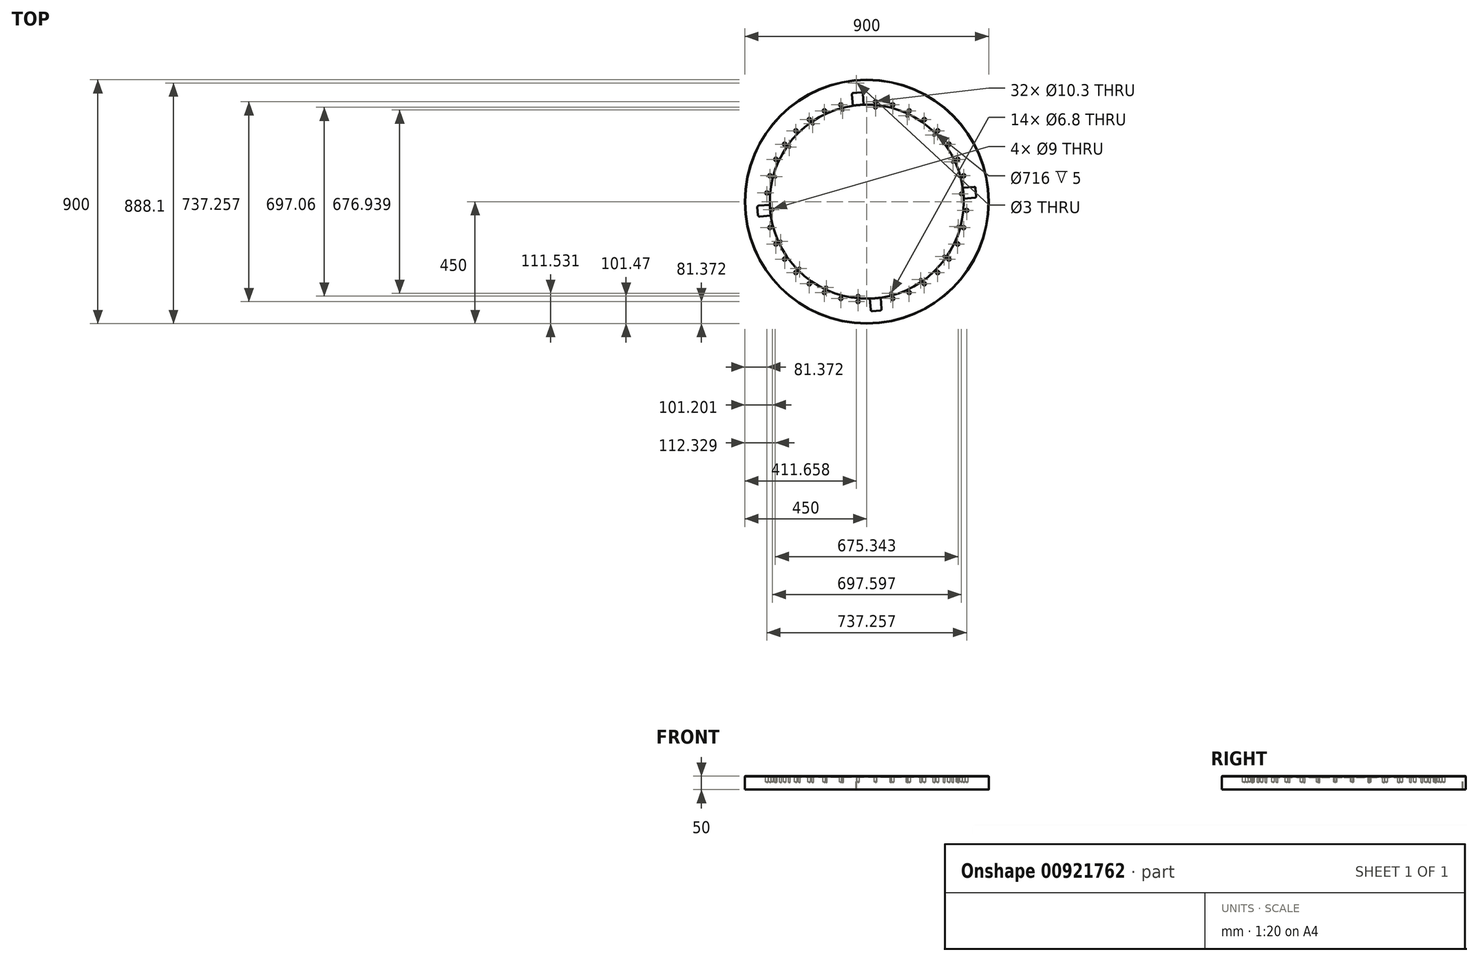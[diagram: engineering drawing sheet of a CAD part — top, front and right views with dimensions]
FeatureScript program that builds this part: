
annotation { "Feature Type Name" : "Feature", "Feature Type Description" : "" }
export const myFeature = defineFeature(function(context is Context, id is Id, definition is map)
    precondition{}
    {
        {
            var Q0;
            Q0=qCreatedBy(makeId("Front.planeOp"),FACE);
            var sketch = newSketch(context, id + "F0", { "sketchPlane" : qUnion([Q0])});
            skLineSegment(sketch, "E0", {"start": v(0, 121.97) * mm, "end": v(0, -124.32) * mm, "construction": true});
            skSolve(sketch);
        }
        {
            var Q0;
            Q0=qCreatedBy(makeId("Top.planeOp"),FACE);
            var sketch = newSketch(context, id + "F1", { "sketchPlane" : qUnion([Q0])});
            skLineSegment(sketch, "E1", {"start": v(-554.57, 0) * mm, "end": v(555.42, 0) * mm, "construction": true});
            skLineSegment(sketch, "E2", {"start": v(0, 588.1) * mm, "end": v(0, -621.05) * mm, "construction": true});
            skSolve(sketch);
        }
        {
            var Q0;
            Q0=qCreatedBy(makeId("Top.planeOp"),FACE);
            var sketch = newSketch(context, id + "F2", { "sketchPlane" : qUnion([Q0])});
            skCircle(sketch, "E3", {"center": v(0, 0) * mm, "radius": 450 * mm});
            skSolve(sketch);
        }
        {
            var Q0;
            Q0 = qSketchRegion(id + "F2", true);
            extrude(context, id + "F3", {"entities" : qUnion([Q0]), "oppositeDirection" : true, "depth" : 50 * mm, "offsetDistance" : 25 * mm});
        }
        {
            var Q0;
            Q0=makeQuery(id+"F3.opExtrude","CAP_FACE",FACE,{"disambiguationData":[OSD([sQuery(id+"F2.wireOp",EDGE,"E3")])],"isStart":true});
            var sketch = newSketch(context, id + "F4", { "sketchPlane" : qUnion([Q0])});
            skCircle(sketch, "E4", {"center": v(0, 0) * mm, "radius": 358 * mm});
            skSolve(sketch);
        }
        {
            var Q0;
            Q0 = qSketchRegion(id + "F4", true);
            extrude(context, id + "F5", {"entities" : qUnion([Q0]), "operationType" : NewBodyOperationType.REMOVE, "oppositeDirection" : true, "depth" : 5 * mm, "offsetDistance" : 25 * mm});
        }
        {
            var Q0;
            Q0=qCreatedBy(makeId("Top.planeOp"),FACE);
            var sketch = newSketch(context, id + "F6", { "sketchPlane" : qUnion([Q0])});
            skCircle(sketch, "E5", {"center": v(32.04, 348.53) * mm, "radius": 4.5 * mm});
            skPoint(sketch, "E6.center", {"position": v(0, 0) * mm});
            skCircle(sketch, "E7.1.0", {"center": v(-89.1, 338.47) * mm, "radius": 4.5 * mm});
            skCircle(sketch, "E7.2.0", {"center": v(-199.49, 287.58) * mm, "radius": 4.5 * mm});
            skCircle(sketch, "E7.3.0", {"center": v(-285.82, 202.01) * mm, "radius": 4.5 * mm});
            skCircle(sketch, "E7.4.0", {"center": v(-337.67, 92.07) * mm, "radius": 4.5 * mm});
            skCircle(sketch, "E7.5.0", {"center": v(-348.8, -28.97) * mm, "radius": 4.5 * mm});
            skCircle(sketch, "E7.6.0", {"center": v(-317.86, -146.52) * mm, "radius": 4.5 * mm});
            skCircle(sketch, "E7.7.0", {"center": v(-248.57, -246.4) * mm, "radius": 4.5 * mm});
            skCircle(sketch, "E7.8.0", {"center": v(-149.31, -316.55) * mm, "radius": 4.5 * mm});
            skCircle(sketch, "E7.9.0", {"center": v(-32.04, -348.53) * mm, "radius": 4.5 * mm});
            skCircle(sketch, "E7.10.0", {"center": v(89.1, -338.47) * mm, "radius": 4.5 * mm});
            skCircle(sketch, "E7.11.0", {"center": v(199.49, -287.58) * mm, "radius": 4.5 * mm});
            skCircle(sketch, "E7.12.0", {"center": v(285.82, -202.01) * mm, "radius": 4.5 * mm});
            skCircle(sketch, "E7.13.0", {"center": v(337.67, -92.07) * mm, "radius": 4.5 * mm});
            skCircle(sketch, "E7.14.0", {"center": v(348.8, 28.97) * mm, "radius": 4.5 * mm});
            skCircle(sketch, "E7.15.0", {"center": v(317.86, 146.52) * mm, "radius": 4.5 * mm});
            skCircle(sketch, "E7.16.0", {"center": v(248.57, 246.4) * mm, "radius": 4.5 * mm});
            skCircle(sketch, "E7.17.0", {"center": v(149.31, 316.55) * mm, "radius": 4.5 * mm});
            skSolve(sketch);
        }
        {
            var Q0;
            Q0=sQuery(id+"F6.wireOp",VERTEX,"E5.center");
            var Q1;
            Q1=sQuery(id+"F6.wireOp",VERTEX,"E7.14.0.center");
            var Q2;
            Q2=sQuery(id+"F6.wireOp",VERTEX,"E7.9.0.center");
            var Q3;
            Q3=sQuery(id+"F6.wireOp",VERTEX,"E7.5.0.center");
            var Q4;
            Q4=makeQuery(id+"F3.opExtrude","SWEPT_BODY",BODY,{"disambiguationData":[OSD([sQuery(id+"F2.wireOp",EDGE,"E3")])]});
            hole(context, id + "F7", {"style" : HoleStyle.C_SINK, "endStyle" : HoleEndStyle.BLIND, "holeDiameter" : 9 * mm, "cSinkDiameter" : 10 * mm, "cSinkAngle" : 90 * degree, "majorDiameter" : 5 * mm, "holeDepth" : 15 * mm, "isTappedThrough" : true, "tappedDepth" : 12 * mm, "tapClearance" : 3, "locations" : qUnion([Q0, Q1, Q2, Q3]), "scope" : qUnion([Q4])});
        }
        {
            var Q0;
            Q0=sQuery(id+"F6.wireOp",VERTEX,"E7.17.0.center");
            var Q1;
            Q1=sQuery(id+"F6.wireOp",VERTEX,"E7.16.0.center");
            var Q2;
            Q2=sQuery(id+"F6.wireOp",VERTEX,"E7.15.0.center");
            var Q3;
            Q3=sQuery(id+"F6.wireOp",VERTEX,"E7.13.0.center");
            var Q4;
            Q4=sQuery(id+"F6.wireOp",VERTEX,"E7.12.0.center");
            var Q5;
            Q5=sQuery(id+"F6.wireOp",VERTEX,"E7.11.0.center");
            var Q6;
            Q6=sQuery(id+"F6.wireOp",VERTEX,"E7.10.0.center");
            var Q7;
            Q7=sQuery(id+"F6.wireOp",VERTEX,"E7.8.0.center");
            var Q8;
            Q8=sQuery(id+"F6.wireOp",VERTEX,"E7.7.0.center");
            var Q9;
            Q9=sQuery(id+"F6.wireOp",VERTEX,"E7.6.0.center");
            var Q10;
            Q10=sQuery(id+"F6.wireOp",VERTEX,"E7.4.0.center");
            var Q11;
            Q11=sQuery(id+"F6.wireOp",VERTEX,"E7.3.0.center");
            var Q12;
            Q12=sQuery(id+"F6.wireOp",VERTEX,"E7.2.0.center");
            var Q13;
            Q13=sQuery(id+"F6.wireOp",VERTEX,"E7.1.0.center");
            var Q14;
            Q14=makeQuery(id+"F3.opExtrude","SWEPT_BODY",BODY,{"disambiguationData":[OSD([sQuery(id+"F2.wireOp",EDGE,"E3")])]});
            hole(context, id + "F8", {"style" : HoleStyle.SIMPLE, "endStyle" : HoleEndStyle.BLIND, "standardTappedOrClearance" : lookupTablePath({ "standard" : "ISO", "engagement" : "75%", "pitch" : "1.25 mm", "size" : "M8", "type" : "Tapped" }), "standardBlindInLast" : lookupTablePath({ "standard" : "ISO", "engagement" : "75%", "pitch" : "1.25 mm", "size" : "M8", "type" : "Tapped" }), "holeDiameter" : 6.8 * mm, "majorDiameter" : 8 * mm, "showTappedDepth" : true, "holeDepth" : 17.75 * mm, "isTappedThrough" : true, "tappedDepth" : 14 * mm, "tapClearance" : 3, "locations" : qUnion([Q0, Q1, Q2, Q3, Q4, Q5, Q6, Q7, Q8, Q9, Q10, Q11, Q12, Q13]), "scope" : qUnion([Q14])});
        }
        {
            var Q0;
            Q0=qCreatedBy(makeId("Top.planeOp"),FACE);
            var sketch = newSketch(context, id + "F9", { "sketchPlane" : qUnion([Q0])});
            skLineSegment(sketch, "E8", {"start": v(0, 0) * mm, "end": v(-54.78, 626.18) * mm, "construction": true});
            skLineSegment(sketch, "E9", {"start": v(0, 0) * mm, "end": v(55.36, 632.75) * mm, "construction": true});
            skSolve(sketch);
        }
        {
            var Q0;
            Q0=sQuery(id+"F9.wireOp",EDGE,"E8");
            cPlane(context, id + "F10", {"entities" : qUnion([Q0]), "cplaneType" : CPlaneType.LINE_ANGLE, "offset" : 25 * mm, "angle" : 90 * degree, "width" : 150 * mm, "height" : 150 * mm});
        }
        {
            var Q0;
            Q0=qCreatedBy(makeId("Top.planeOp"),FACE);
            var sketch = newSketch(context, id + "F11", { "sketchPlane" : qUnion([Q0])});
            skLineSegment(sketch, "E10", {"start": v(0, 0) * mm, "end": v(-63.03, 720.46) * mm, "construction": true});
            skSolve(sketch);
        }
        {
            var Q0;
            Q0=qCreatedBy(makeId("Top.planeOp"),FACE);
            var sketch = newSketch(context, id + "F12", { "sketchPlane" : qUnion([Q0])});
            skLineSegment(sketch, "E11", {"start": v(-14.84, 399.23) * mm, "end": v(-11.22, 357.82) * mm});
            skLineSegment(sketch, "E12", {"start": v(-35.21, 402.46) * mm, "end": v(-31.2, 356.64) * mm});
            skArc(sketch, "E13", {"start": v(-11.22, 357.82) * mm, "mid": v(-21.22, 357.37) * mm, "end": v(-31.2, 356.64) * mm});
            skLineSegment(sketch, "E14", {"start": v(-35.21, 402.46) * mm, "end": v(-20.26, 403.77) * mm});
            skLineSegment(sketch, "E15.MirrorCS", {"start": v(-35.21, 402.46) * mm, "end": v(-50.16, 401.15) * mm});
            skLineSegment(sketch, "E16.MirrorCS", {"start": v(-54.7, 395.74) * mm, "end": v(-51.09, 354.34) * mm});
            skArc(sketch, "E17.MirrorCS", {"start": v(-51.09, 354.34) * mm, "mid": v(-41.16, 355.63) * mm, "end": v(-31.2, 356.64) * mm});
            skArc(sketch, "E18.1.0", {"start": v(-357.82, -11.22) * mm, "mid": v(-357.37, -21.22) * mm, "end": v(-356.64, -31.2) * mm});
            skLineSegment(sketch, "E18.1.1", {"start": v(-399.23, -14.84) * mm, "end": v(-357.82, -11.22) * mm});
            skLineSegment(sketch, "E18.1.2", {"start": v(-402.46, -35.21) * mm, "end": v(-403.77, -20.26) * mm});
            skLineSegment(sketch, "E18.1.3", {"start": v(-402.46, -35.21) * mm, "end": v(-356.64, -31.2) * mm});
            skLineSegment(sketch, "E18.1.4", {"start": v(-402.46, -35.21) * mm, "end": v(-401.15, -50.16) * mm});
            skLineSegment(sketch, "E18.1.5", {"start": v(-395.74, -54.7) * mm, "end": v(-354.34, -51.09) * mm});
            skArc(sketch, "E18.1.6", {"start": v(-354.34, -51.09) * mm, "mid": v(-355.63, -41.16) * mm, "end": v(-356.64, -31.2) * mm});
            skArc(sketch, "E18.2.0", {"start": v(11.22, -357.82) * mm, "mid": v(21.22, -357.37) * mm, "end": v(31.2, -356.64) * mm});
            skLineSegment(sketch, "E18.2.1", {"start": v(14.84, -399.23) * mm, "end": v(11.22, -357.82) * mm});
            skLineSegment(sketch, "E18.2.2", {"start": v(35.21, -402.46) * mm, "end": v(20.26, -403.77) * mm});
            skLineSegment(sketch, "E18.2.3", {"start": v(35.21, -402.46) * mm, "end": v(31.2, -356.64) * mm});
            skLineSegment(sketch, "E18.2.4", {"start": v(35.21, -402.46) * mm, "end": v(50.16, -401.15) * mm});
            skLineSegment(sketch, "E18.2.5", {"start": v(54.7, -395.74) * mm, "end": v(51.09, -354.34) * mm});
            skArc(sketch, "E18.2.6", {"start": v(51.09, -354.34) * mm, "mid": v(41.16, -355.63) * mm, "end": v(31.2, -356.64) * mm});
            skArc(sketch, "E18.3.0", {"start": v(357.82, 11.22) * mm, "mid": v(357.37, 21.22) * mm, "end": v(356.64, 31.2) * mm});
            skLineSegment(sketch, "E18.3.1", {"start": v(399.23, 14.84) * mm, "end": v(357.82, 11.22) * mm});
            skLineSegment(sketch, "E18.3.2", {"start": v(402.46, 35.21) * mm, "end": v(403.77, 20.26) * mm});
            skLineSegment(sketch, "E18.3.3", {"start": v(402.46, 35.21) * mm, "end": v(356.64, 31.2) * mm});
            skLineSegment(sketch, "E18.3.4", {"start": v(402.46, 35.21) * mm, "end": v(401.15, 50.16) * mm});
            skLineSegment(sketch, "E18.3.5", {"start": v(395.74, 54.7) * mm, "end": v(354.34, 51.09) * mm});
            skArc(sketch, "E18.3.6", {"start": v(354.34, 51.09) * mm, "mid": v(355.63, 41.16) * mm, "end": v(356.64, 31.2) * mm});
            skPoint(sketch, "E19.visualSharp", {"position": v(-55.14, 400.72) * mm});
            skArc(sketch, "E19.filletArc", {"start": v(-50.16, 401.15) * mm, "mid": v(-53.56, 399.39) * mm, "end": v(-54.7, 395.74) * mm});
            skPoint(sketch, "E20.visualSharp", {"position": v(-15.28, 404.2) * mm});
            skArc(sketch, "E20.filletArc", {"start": v(-14.84, 399.23) * mm, "mid": v(-16.6, 402.62) * mm, "end": v(-20.26, 403.77) * mm});
            skPoint(sketch, "E21.visualSharp", {"position": v(-400.72, -55.14) * mm});
            skArc(sketch, "E21.filletArc", {"start": v(-401.15, -50.16) * mm, "mid": v(-399.39, -53.56) * mm, "end": v(-395.74, -54.7) * mm});
            skPoint(sketch, "E22.visualSharp", {"position": v(-404.2, -15.28) * mm});
            skArc(sketch, "E22.filletArc", {"start": v(-399.23, -14.84) * mm, "mid": v(-402.62, -16.6) * mm, "end": v(-403.77, -20.26) * mm});
            skPoint(sketch, "E23.visualSharp", {"position": v(15.28, -404.2) * mm});
            skArc(sketch, "E23.filletArc", {"start": v(14.84, -399.23) * mm, "mid": v(16.6, -402.62) * mm, "end": v(20.26, -403.77) * mm});
            skPoint(sketch, "E24.visualSharp", {"position": v(55.14, -400.72) * mm});
            skArc(sketch, "E24.filletArc", {"start": v(50.16, -401.15) * mm, "mid": v(53.56, -399.39) * mm, "end": v(54.7, -395.74) * mm});
            skPoint(sketch, "E25.visualSharp", {"position": v(400.72, 55.14) * mm});
            skArc(sketch, "E25.filletArc", {"start": v(401.15, 50.16) * mm, "mid": v(399.39, 53.56) * mm, "end": v(395.74, 54.7) * mm});
            skPoint(sketch, "E26.visualSharp", {"position": v(404.2, 15.28) * mm});
            skArc(sketch, "E26.filletArc", {"start": v(399.23, 14.84) * mm, "mid": v(402.62, 16.6) * mm, "end": v(403.77, 20.26) * mm});
            skSolve(sketch);
        }
        {
            var Q0;
            Q0 = qSketchRegion(id + "F12", true);
            extrude(context, id + "F13", {"entities" : qUnion([Q0]), "operationType" : NewBodyOperationType.REMOVE, "oppositeDirection" : true, "depth" : 2 * mm, "offsetDistance" : 25 * mm});
        }
        {
            var Q0;
            Q0=makeQuery(id+"F4.imprint","IMPRINT",FACE,{"disambiguationData":[TD([[makeQuery(id+"F4.imprint","IMPRINT",EDGE,{"derivedFrom":sQuery(id+"F4.wireOp",EDGE,"E4")}),-1.0]])]});
            var sketch = newSketch(context, id + "F14", { "sketchPlane" : qUnion([Q0])});
            skCircle(sketch, "E27", {"center": v(-38.34, 438.1) * mm, "radius": 1.5 * mm});
            skSolve(sketch);
        }
        {
            var Q0;
            Q0 = qSketchRegion(id + "F14", true);
            extrude(context, id + "F15", {"entities" : qUnion([Q0]), "operationType" : NewBodyOperationType.REMOVE, "oppositeDirection" : true, "depth" : 60.1 * mm, "offsetDistance" : 25 * mm});
        }
        {
            var Q0;
            Q0=qCreatedBy(makeId("Top.planeOp"),FACE);
            var sketch = newSketch(context, id + "F16", { "sketchPlane" : qUnion([Q0])});
            skCircle(sketch, "E28", {"center": v(32.25, 368.63) * mm, "radius": 6 * mm});
            skCircle(sketch, "E29.2.0", {"center": v(-95.77, 357.43) * mm, "radius": 6 * mm});
            skCircle(sketch, "E29.3.0", {"center": v(-156.38, 335.37) * mm, "radius": 6 * mm});
            skCircle(sketch, "E29.4.0", {"center": v(-212.24, 303.12) * mm, "radius": 6 * mm});
            skCircle(sketch, "E29.5.0", {"center": v(-261.66, 261.66) * mm, "radius": 6 * mm});
            skCircle(sketch, "E29.6.0", {"center": v(-303.12, 212.24) * mm, "radius": 6 * mm});
            skCircle(sketch, "E29.7.0", {"center": v(-335.37, 156.38) * mm, "radius": 6 * mm});
            skCircle(sketch, "E29.8.0", {"center": v(-357.43, 95.77) * mm, "radius": 6 * mm});
            skCircle(sketch, "E29.9.0", {"center": v(-368.63, 32.25) * mm, "radius": 6 * mm});
            skCircle(sketch, "E29.11.0", {"center": v(-357.43, -95.77) * mm, "radius": 6 * mm});
            skCircle(sketch, "E29.12.0", {"center": v(-335.37, -156.38) * mm, "radius": 6 * mm});
            skCircle(sketch, "E29.13.0", {"center": v(-303.12, -212.24) * mm, "radius": 6 * mm});
            skCircle(sketch, "E29.14.0", {"center": v(-261.66, -261.66) * mm, "radius": 6 * mm});
            skCircle(sketch, "E29.15.0", {"center": v(-212.24, -303.12) * mm, "radius": 6 * mm});
            skCircle(sketch, "E29.16.0", {"center": v(-156.38, -335.37) * mm, "radius": 6 * mm});
            skCircle(sketch, "E29.17.0", {"center": v(-95.77, -357.43) * mm, "radius": 6 * mm});
            skCircle(sketch, "E29.18.0", {"center": v(-32.25, -368.63) * mm, "radius": 6 * mm});
            skCircle(sketch, "E29.20.0", {"center": v(95.77, -357.43) * mm, "radius": 6 * mm});
            skCircle(sketch, "E29.21.0", {"center": v(156.38, -335.37) * mm, "radius": 6 * mm});
            skCircle(sketch, "E29.22.0", {"center": v(212.24, -303.12) * mm, "radius": 6 * mm});
            skCircle(sketch, "E29.23.0", {"center": v(261.66, -261.66) * mm, "radius": 6 * mm});
            skCircle(sketch, "E29.24.0", {"center": v(303.12, -212.24) * mm, "radius": 6 * mm});
            skCircle(sketch, "E29.25.0", {"center": v(335.37, -156.38) * mm, "radius": 6 * mm});
            skCircle(sketch, "E29.26.0", {"center": v(357.43, -95.77) * mm, "radius": 6 * mm});
            skCircle(sketch, "E29.27.0", {"center": v(368.63, -32.25) * mm, "radius": 6 * mm});
            skCircle(sketch, "E29.29.0", {"center": v(357.43, 95.77) * mm, "radius": 6 * mm});
            skCircle(sketch, "E29.30.0", {"center": v(335.37, 156.38) * mm, "radius": 6 * mm});
            skCircle(sketch, "E29.31.0", {"center": v(303.12, 212.24) * mm, "radius": 6 * mm});
            skCircle(sketch, "E29.32.0", {"center": v(261.66, 261.66) * mm, "radius": 6 * mm});
            skCircle(sketch, "E29.33.0", {"center": v(212.24, 303.12) * mm, "radius": 6 * mm});
            skCircle(sketch, "E29.34.0", {"center": v(156.38, 335.37) * mm, "radius": 6 * mm});
            skCircle(sketch, "E29.35.0", {"center": v(95.77, 357.43) * mm, "radius": 6 * mm});
            skPoint(sketch, "E29.center", {"position": v(0, 0) * mm});
            skSolve(sketch);
        }
        {
            var Q0;
            Q0=sQuery(id+"F16.wireOp",VERTEX,"E29.34.0.center");
            var Q1;
            Q1=sQuery(id+"F16.wireOp",VERTEX,"E28.center");
            var Q2;
            Q2=sQuery(id+"F16.wireOp",VERTEX,"E29.35.0.center");
            var Q3;
            Q3=sQuery(id+"F16.wireOp",VERTEX,"E29.33.0.center");
            var Q4;
            Q4=sQuery(id+"F16.wireOp",VERTEX,"E29.32.0.center");
            var Q5;
            Q5=sQuery(id+"F16.wireOp",VERTEX,"E29.31.0.center");
            var Q6;
            Q6=sQuery(id+"F16.wireOp",VERTEX,"E29.30.0.center");
            var Q7;
            Q7=sQuery(id+"F16.wireOp",VERTEX,"E29.29.0.center");
            var Q8;
            Q8=sQuery(id+"F16.wireOp",VERTEX,"E29.27.0.center");
            var Q9;
            Q9=sQuery(id+"F16.wireOp",VERTEX,"E29.26.0.center");
            var Q10;
            Q10=sQuery(id+"F16.wireOp",VERTEX,"E29.25.0.center");
            var Q11;
            Q11=sQuery(id+"F16.wireOp",VERTEX,"E29.24.0.center");
            var Q12;
            Q12=sQuery(id+"F16.wireOp",VERTEX,"E29.20.0.center");
            var Q13;
            Q13=sQuery(id+"F16.wireOp",VERTEX,"E29.21.0.center");
            var Q14;
            Q14=sQuery(id+"F16.wireOp",VERTEX,"E29.22.0.center");
            var Q15;
            Q15=sQuery(id+"F16.wireOp",VERTEX,"E29.23.0.center");
            var Q16;
            Q16=sQuery(id+"F16.wireOp",VERTEX,"E29.18.0.center");
            var Q17;
            Q17=sQuery(id+"F16.wireOp",VERTEX,"E29.17.0.center");
            var Q18;
            Q18=sQuery(id+"F16.wireOp",VERTEX,"E29.16.0.center");
            var Q19;
            Q19=sQuery(id+"F16.wireOp",VERTEX,"E29.15.0.center");
            var Q20;
            Q20=sQuery(id+"F16.wireOp",VERTEX,"E29.14.0.center");
            var Q21;
            Q21=sQuery(id+"F16.wireOp",VERTEX,"E29.13.0.center");
            var Q22;
            Q22=sQuery(id+"F16.wireOp",VERTEX,"E29.12.0.center");
            var Q23;
            Q23=sQuery(id+"F16.wireOp",VERTEX,"E29.11.0.center");
            var Q24;
            Q24=sQuery(id+"F16.wireOp",VERTEX,"E29.9.0.center");
            var Q25;
            Q25=sQuery(id+"F16.wireOp",VERTEX,"E29.8.0.center");
            var Q26;
            Q26=sQuery(id+"F16.wireOp",VERTEX,"E29.7.0.center");
            var Q27;
            Q27=sQuery(id+"F16.wireOp",VERTEX,"E29.6.0.center");
            var Q28;
            Q28=sQuery(id+"F16.wireOp",VERTEX,"E29.5.0.center");
            var Q29;
            Q29=sQuery(id+"F16.wireOp",VERTEX,"E29.4.0.center");
            var Q30;
            Q30=sQuery(id+"F16.wireOp",VERTEX,"E29.3.0.center");
            var Q31;
            Q31=sQuery(id+"F16.wireOp",VERTEX,"E29.2.0.center");
            var Q32;
            Q32=makeQuery(id+"F3.opExtrude","SWEPT_BODY",BODY,{"disambiguationData":[OSD([sQuery(id+"F2.wireOp",EDGE,"E3")])]});
            hole(context, id + "F17", {"style" : HoleStyle.C_SINK, "endStyle" : HoleEndStyle.BLIND, "holeDiameter" : 10.3 * mm, "cSinkDiameter" : 12.5 * mm, "cSinkAngle" : 90 * degree, "majorDiameter" : 12 * mm, "holeDepth" : 21.25 * mm, "isTappedThrough" : true, "tappedDepth" : 16 * mm, "tapClearance" : 3, "startFromSketch" : true, "locations" : qUnion([Q0, Q1, Q2, Q3, Q4, Q5, Q6, Q7, Q8, Q9, Q10, Q11, Q12, Q13, Q14, Q15, Q16, Q17, Q18, Q19, Q20, Q21, Q22, Q23, Q24, Q25, Q26, Q27, Q28, Q29, Q30, Q31]), "scope" : qUnion([Q32])});
        }
        {
            var Q0;
            Q0=makeQuery(id+"F3.opExtrude","CAP_EDGE",EDGE,{"disambiguationData":[OSD([sQuery(id+"F2.wireOp",EDGE,"E3")])],"isStart":true});
            var Q1;
            Q1=makeQuery(id+"F3.opExtrude","CAP_EDGE",EDGE,{"disambiguationData":[OSD([sQuery(id+"F2.wireOp",EDGE,"E3")])],"isStart":false});
            chamfer(context, id + "F18", {"entities" : qUnion([Q0, Q1]), "width" : 1 * mm, "tangentPropagation" : true});
        }
    });
